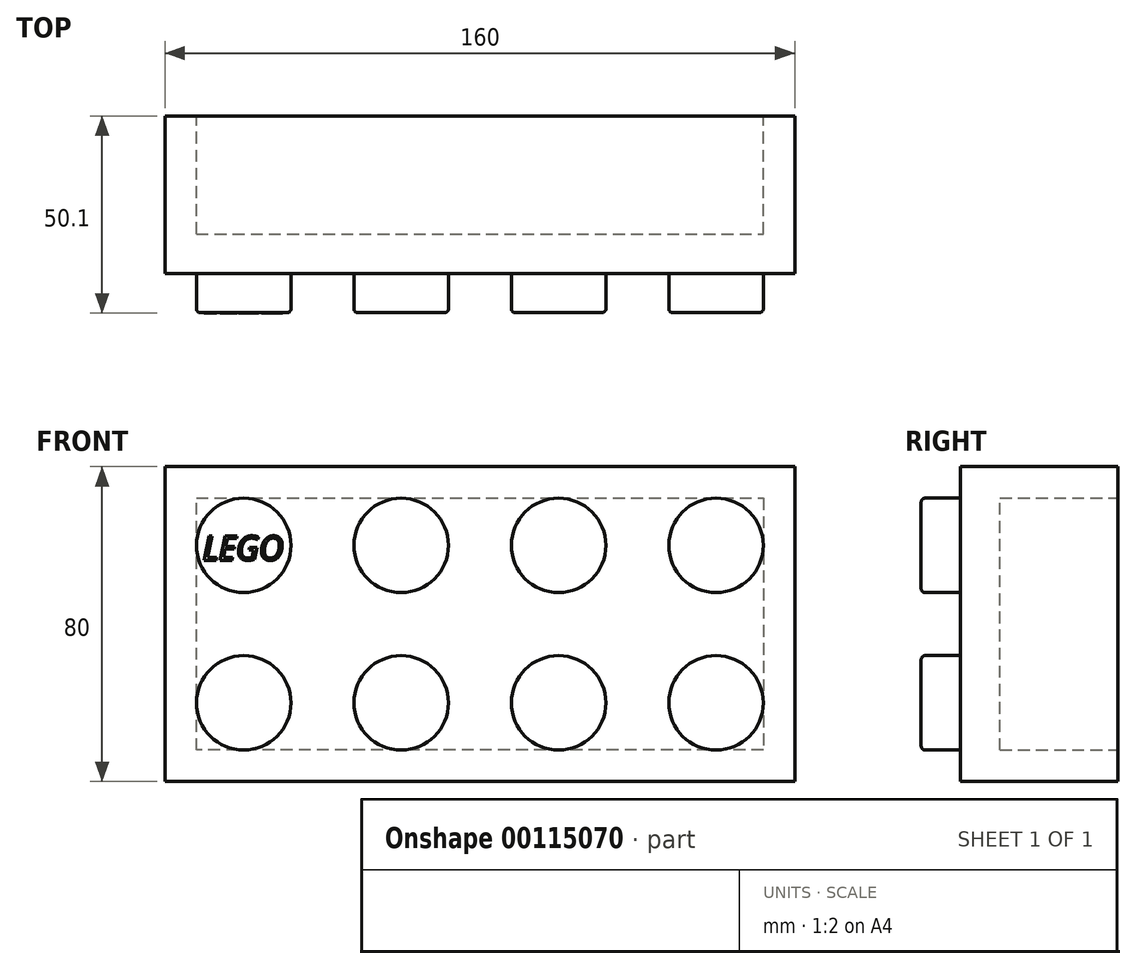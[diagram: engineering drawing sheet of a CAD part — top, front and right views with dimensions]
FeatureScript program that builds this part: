
annotation { "Feature Type Name" : "Feature", "Feature Type Description" : "" }
export const myFeature = defineFeature(function(context is Context, id is Id, definition is map)
    precondition{}
    {
        {
            var Q0;
            Q0=qCreatedBy(makeId("Front.planeOp"),FACE);
            var sketch = newSketch(context, id + "F0", { "sketchPlane" : qUnion([Q0])});
            skLineSegment(sketch, "E0.bottom", {"start": v(-69.19, 23.77) * mm, "end": v(90.81, 23.77) * mm});
            skLineSegment(sketch, "E0.top", {"start": v(-69.19, -56.23) * mm, "end": v(90.81, -56.23) * mm});
            skLineSegment(sketch, "E0.left", {"start": v(-69.19, 23.77) * mm, "end": v(-69.19, -56.23) * mm});
            skLineSegment(sketch, "E0.right", {"start": v(90.81, 23.77) * mm, "end": v(90.81, -56.23) * mm});
            skSolve(sketch);
        }
        {
            var Q0;
            Q0 = qSketchRegion(id + "F0", true);
            extrude(context, id + "F1", {"entities" : qUnion([Q0]), "depth" : 40 * mm});
        }
        {
            var Q0;
            Q0=makeQuery(id+"F1.opExtrude","CAP_FACE",FACE,{"disambiguationData":[OSD([sQuery(id+"F0.wireOp",EDGE,"E0.bottom"),sQuery(id+"F0.wireOp",EDGE,"E0.top"),sQuery(id+"F0.wireOp",EDGE,"E0.left"),sQuery(id+"F0.wireOp",EDGE,"E0.right")])],"isStart":true});
            var sketch = newSketch(context, id + "F2", { "sketchPlane" : qUnion([Q0])});
            skLineSegment(sketch, "E1.0", {"start": v(61.19, 15.77) * mm, "end": v(-82.81, 15.77) * mm});
            skLineSegment(sketch, "E1.1", {"start": v(61.19, -48.23) * mm, "end": v(61.19, 15.77) * mm});
            skLineSegment(sketch, "E1.2", {"start": v(-82.81, -48.23) * mm, "end": v(61.19, -48.23) * mm});
            skLineSegment(sketch, "E1.3", {"start": v(-82.81, 15.77) * mm, "end": v(-82.81, -48.23) * mm});
            skSolve(sketch);
        }
        {
            var Q0;
            Q0=makeQuery(id+"F2.imprint","IMPRINT",FACE,{"disambiguationData":[TD([[makeQuery(id+"F2.imprint","IMPRINT",EDGE,{"derivedFrom":sQuery(id+"F2.wireOp",EDGE,"E1.0")}),1.0]])]});
            extrude(context, id + "F3", {"entities" : qUnion([Q0]), "operationType" : NewBodyOperationType.REMOVE, "oppositeDirection" : true, "depth" : 30 * mm});
        }
        {
            var Q0;
            Q0=makeQuery(id+"F1.opExtrude","CAP_FACE",FACE,{"disambiguationData":[OSD([sQuery(id+"F0.wireOp",EDGE,"E0.bottom"),sQuery(id+"F0.wireOp",EDGE,"E0.top"),sQuery(id+"F0.wireOp",EDGE,"E0.left"),sQuery(id+"F0.wireOp",EDGE,"E0.right")])],"isStart":false});
            var sketch = newSketch(context, id + "F4", { "sketchPlane" : qUnion([Q0])});
            skCircle(sketch, "E2", {"center": v(-49.19, 3.77) * mm, "radius": 12 * mm});
            skCircle(sketch, "E3.0.1.0", {"center": v(-49.19, -36.23) * mm, "radius": 12 * mm});
            skCircle(sketch, "E3.1.0.0", {"center": v(-9.19, 3.77) * mm, "radius": 12 * mm});
            skCircle(sketch, "E3.1.1.0", {"center": v(-9.19, -36.23) * mm, "radius": 12 * mm});
            skCircle(sketch, "E3.2.0.0", {"center": v(30.81, 3.77) * mm, "radius": 12 * mm});
            skCircle(sketch, "E3.2.1.0", {"center": v(30.81, -36.23) * mm, "radius": 12 * mm});
            skCircle(sketch, "E3.3.0.0", {"center": v(70.81, 3.77) * mm, "radius": 12 * mm});
            skCircle(sketch, "E3.3.1.0", {"center": v(70.81, -36.23) * mm, "radius": 12 * mm});
            skLineSegment(sketch, "E3.direction1", {"start": v(-49.19, 3.77) * mm, "end": v(-9.19, 3.77) * mm, "construction": true});
            skLineSegment(sketch, "E3.direction2", {"start": v(-49.19, 3.77) * mm, "end": v(-49.19, -36.23) * mm, "construction": true});
            skSolve(sketch);
        }
        {
            var Q0;
            Q0 = qSketchRegion(id + "F4", true);
            extrude(context, id + "F5", {"entities" : qUnion([Q0]), "operationType" : NewBodyOperationType.ADD, "depth" : 10 * mm});
        }
        {
            var Q0;
            Q0=makeQuery(id+"F5.opExtrude","CAP_FACE",FACE,{"disambiguationData":[OSD([sQuery(id+"F4.wireOp",EDGE,"E3.0.1.0")])],"isStart":false});
            var Q1;
            Q1=makeQuery(id+"F5.opExtrude","CAP_FACE",FACE,{"disambiguationData":[OSD([sQuery(id+"F4.wireOp",EDGE,"E2")])],"isStart":false});
            var Q2;
            Q2=makeQuery(id+"F5.opExtrude","CAP_FACE",FACE,{"disambiguationData":[OSD([sQuery(id+"F4.wireOp",EDGE,"E3.1.1.0")])],"isStart":false});
            var Q3;
            Q3=makeQuery(id+"F5.opExtrude","CAP_FACE",FACE,{"disambiguationData":[OSD([sQuery(id+"F4.wireOp",EDGE,"E3.1.0.0")])],"isStart":false});
            var Q4;
            Q4=makeQuery(id+"F5.opExtrude","CAP_FACE",FACE,{"disambiguationData":[OSD([sQuery(id+"F4.wireOp",EDGE,"E3.2.1.0")])],"isStart":false});
            var Q5;
            Q5=makeQuery(id+"F5.opExtrude","CAP_FACE",FACE,{"disambiguationData":[OSD([sQuery(id+"F4.wireOp",EDGE,"E3.2.0.0")])],"isStart":false});
            var Q6;
            Q6=makeQuery(id+"F5.opExtrude","CAP_FACE",FACE,{"disambiguationData":[OSD([sQuery(id+"F4.wireOp",EDGE,"E3.3.0.0")])],"isStart":false});
            var Q7;
            Q7=makeQuery(id+"F5.opExtrude","CAP_FACE",FACE,{"disambiguationData":[OSD([sQuery(id+"F4.wireOp",EDGE,"E3.3.1.0")])],"isStart":false});
            fillet(context, id + "F6", {"entities" : qUnion([Q0, Q1, Q2, Q3, Q4, Q5, Q6, Q7]), "radius" : 1 * mm, "tangentPropagation" : true, "allowEdgeOverflow" : false});
        }
        {
            var Q0;
            Q0=makeQuery(id+"F5.opExtrude","CAP_FACE",FACE,{"disambiguationData":[OSD([sQuery(id+"F4.wireOp",EDGE,"E2")])],"isStart":false});
            var sketch = newSketch(context, id + "F7", { "sketchPlane" : qUnion([Q0])});
            skText(sketch, "E4", { "text": "LEGO", "fontName": "OpenSans-Italic.ttf"});
            const initialGuessF7  = {"E4": [-0.05965, 0, 1, 0, 0.0062]};
            skSetInitialGuess(sketch, initialGuessF7);
            skSolve(sketch);
        }
        {
            var Q0;
            Q0 = qSketchRegion(id + "F7", true);
            extrude(context, id + "F8", {"entities" : qUnion([Q0]), "operationType" : NewBodyOperationType.ADD, "depth" : 0.1 * mm});
        }
    });
